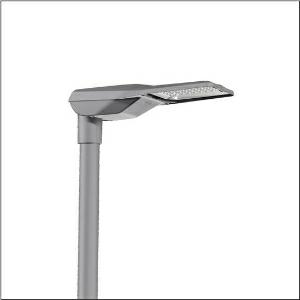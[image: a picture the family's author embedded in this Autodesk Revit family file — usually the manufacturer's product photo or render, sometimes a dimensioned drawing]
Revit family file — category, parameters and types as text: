
# Revit family: streetlight_sl_21_iq_mini___pl52_5xe2h41d08gb_a481
name_source: partatom
category: Lighting Fixtures
units: mm (PartAtom-declared; Revit-internal decimal feet)

## family parameters
Cut with Voids When Loaded = No
Host = Face
Light Source = No
Part Type = Normal
Room Calculation Point = No
Round Connector Dimension = Use Diameter
Shared = No

## types (1)
- --- (1 x LED, 5810 lm, 37.1 W, 4000K)
    Apparent Load = 37 VA
    CIE Flux Codes = 27 59 98 100 100
    Color Rendering = 70
    Color Temperature = 4000K
    Default Elevation = 1800 mm
    Description = Streetlight SL 21 iQ mini, mast luminaire, primary light control with lens, of PMMA, primary optical cover: cover, of toughened safety glass, transparent, light distribution: PL52, light emission: direct distribution, primary light characteristic: asymmetric, installation type: post-top, side-entry, LED, High Power LED, rated luminous flux: 5.810lm, luminous efficacy: 157lm/W, light colour: 740, colour temperature: 4000K, control gear: iQ-Comfort, control: Auto-Match, Temp-Guard, Lumen-Switch, Night-Set, Smart-Wire, Light-Fading, Desk-Remote (wireless, voltage-free reading and setting of iQ features in the workshop via application-optimized NFC function/RFID function), optimised constant luminous flux control (CLO 2.0), pre-setting: linear dimming characteristic, mains connection: 220..240V, AC, 50/60Hz, start of lifetime: 37W, end of service life: 39W, reduction: 18W, luminaire housing, of diecast aluminium, powder-coated, Siteco® metallic grey (DB 702S), corrosivity category C5 mid according to DIN EN ISO 12944, please order mast flange separately, inclination adjustable: 0°, 5°, 10°, 15°, sealing non-destructively replaceable, multi-level sealing system, length: 628mm, width: 235mm, height: 110mm, mast flange for spigot size: 42mm (side-entry): 5XC10008XM4, 60/48mm (side-entry/post-top): 5XC10108XM2, 76/60mm (side-entry/post-top): 5XC10108XM1, mounting height: 4..8m, protection rating (complete): IP66, insulation class (complete): insulation class II (safety insulation), certification: CE, ENEC, ENEC+, VDE, impact resistance: IK10, permissible operating ambient temperature for outdoor applications: -40..+50°C, standard-compliant lighting for roads and squares, packaging unit: 1 piece

Light Distribution: PL52
    Height = 110 mm
    Lamp = 1 x LED
    Lamp Light Flux = 5810 lm
    Lamp Power = 37.1 W
    Lamp count = 1
    Length = 625 mm
    Luminous efficacy = 157 lm/W
    Manufacturer = Siteco
    ModVariant = No
    Model = 5XE2H41D08GB
    Number of Poles = 1
    OnlyDefault = Yes
    Power Factor = 1
    Product Name = Streetlight SL 21 iQ mini | PL52
    Product group = mast luminaire | pylon top
    ProductGroupID = 6100
    Protection Class = Protection class II
    Protection Degree = IP 66
    RLX_Detail_Level = 1
    RLX_Emergency_Light_Flux = 0 lm
    RLX_Emergency_Type = 0
    RLX_Emergency_Type_DB = No
    RlxData = <blob elided: 36009 chars, md5=966d7070>
    Socket = socket
    Standby Power = 0 W
    System Light Flux = 5810 lm
    System Power = 37 W
    Type Comments = factory setting: luminous flux: 100 % | dim-lin: 254 | 385 mA
    Type Image = l_1003519.jpg
    URL = http://relux.com
    VarID = @adj_211581
    Voltage = 0 V
    Weight = 0.00 kg
    Width = 234 mm

## geometry (parser evidence)
native form markers: Blend x4, Sweep x11
no freeform markers — native parametric forms only
